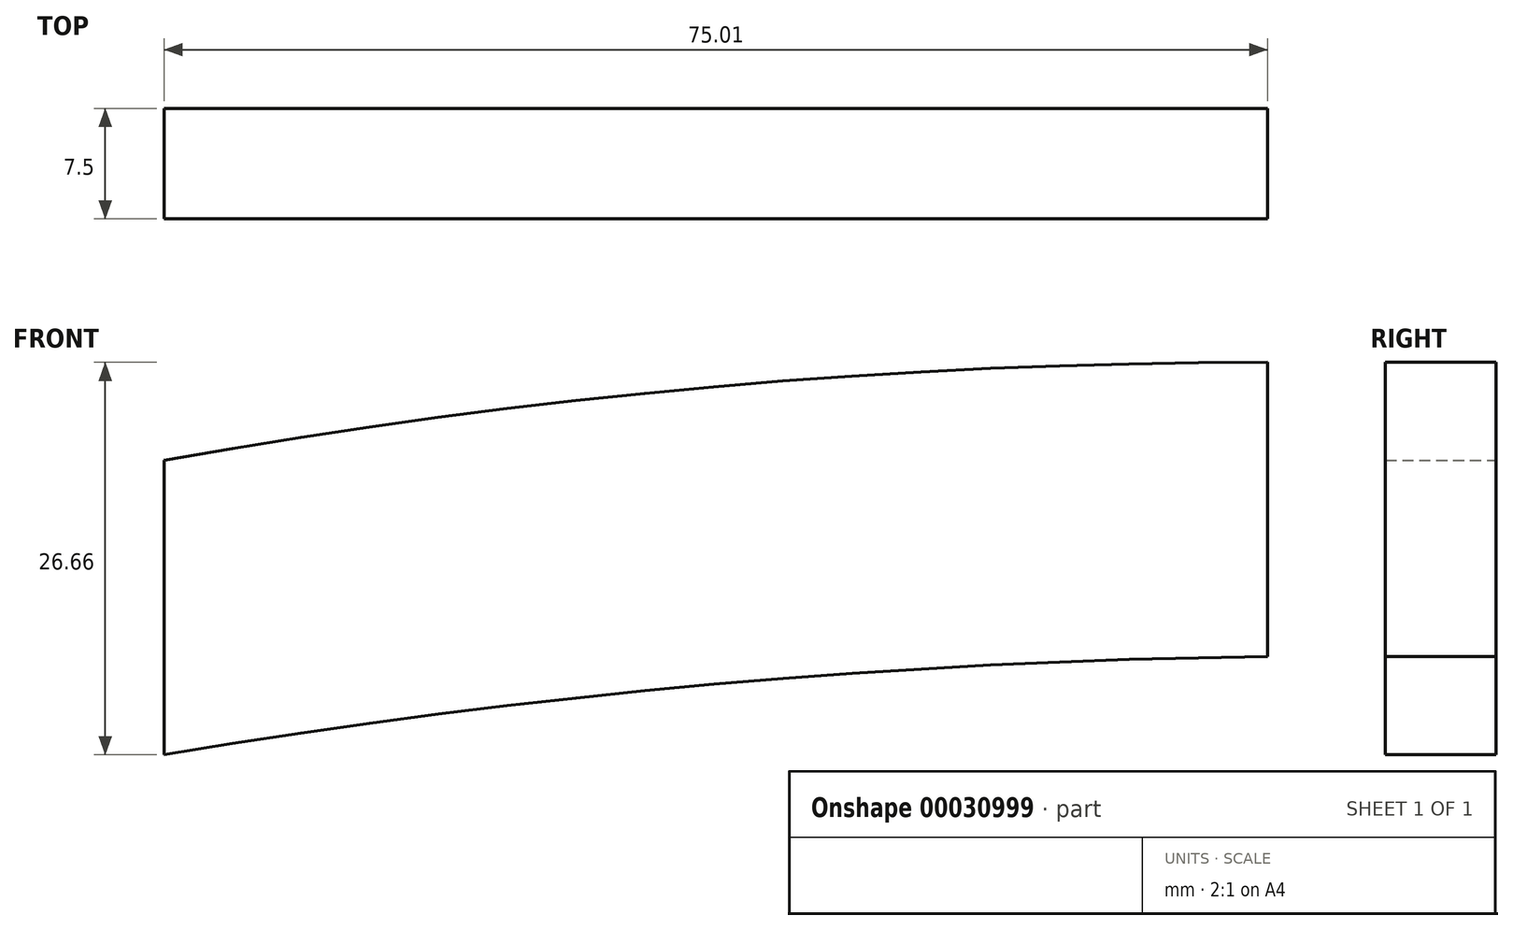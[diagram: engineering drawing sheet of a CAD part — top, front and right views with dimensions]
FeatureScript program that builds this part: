
annotation { "Feature Type Name" : "Feature", "Feature Type Description" : "" }
export const myFeature = defineFeature(function(context is Context, id is Id, definition is map)
    precondition{}
    {
        {
            var Q0;
            Q0=qCreatedBy(makeId("Front.planeOp"),FACE);
            var sketch = newSketch(context, id + "F0", { "sketchPlane" : qUnion([Q0])});
            skLineSegment(sketch, "E0", {"start": v(-74.63, 0.78) * mm, "end": v(-74.63, 20.78) * mm});
            skArc(sketch, "E1", {"start": v(0.38, 27.44) * mm, "mid": v(-37.27, 25.78) * mm, "end": v(-74.63, 20.78) * mm});
            skLineSegment(sketch, "E2", {"start": v(0.38, 27.44) * mm, "end": v(0.38, 7.44) * mm});
            skArc(sketch, "E3", {"start": v(0.38, 7.44) * mm, "mid": v(-37.25, 5.56) * mm, "end": v(-74.63, 0.78) * mm});
            skSolve(sketch);
        }
        {
            var Q0;
            Q0=makeQuery(id+"F0.imprint","IMPRINT",FACE,{"disambiguationData":[TD([[makeQuery(id+"F0.imprint","IMPRINT",EDGE,{"derivedFrom":sQuery(id+"F0.wireOp",EDGE,"E0")}),-1.0]])]});
            extrude(context, id + "F1", {"entities" : qUnion([Q0]), "depth" : 7.5 * mm});
        }
    });
